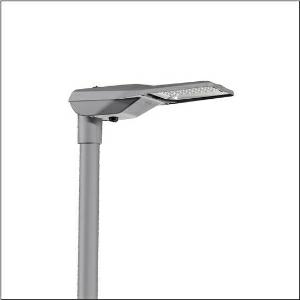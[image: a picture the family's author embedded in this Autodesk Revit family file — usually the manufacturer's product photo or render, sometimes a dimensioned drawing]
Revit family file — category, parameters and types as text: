
# Revit family: streetlight_sl_21_iq_mini___st1_0a_5xe2d21y08hb_5d36
name_source: partatom
category: Lighting Fixtures
units: mm (PartAtom-declared; Revit-internal decimal feet)

## family parameters
Cut with Voids When Loaded = No
Host = Face
Light Source = No
Part Type = Normal
Room Calculation Point = No
Round Connector Dimension = Use Diameter
Shared = No

## types (1)
- --- (1 x LED, 7820 lm, 71 W, 2200K)
    Apparent Load = 71 VA
    CIE Flux Codes = 37 72 97 100 100
    Color Rendering = 70
    Color Temperature = 2200K
    Default Elevation = 1800 mm
    Description = Streetlight SL 21 iQ mini, mast luminaire, primary light control with lens, of PMMA, primary optical cover: cover, of toughened safety glass, transparent, light distribution: ST1.0a, light emission: direct distribution, primary light characteristic: asymmetric, installation type: post-top, side-entry, LED, High Power LED, rated luminous flux: 7.820lm, luminous efficacy: 110lm/W, light colour: 722, colour temperature: 2200K, control gear: iQ-Street Remote, D4i with power reduction, control: pre-setting: logarithmic dimming characteristic, Street-Remote, Auto-Match, Temp-Guard, Lumen-Switch, Night-Set, Smart-Wire, Light-Fading, Desk-Remote (wireless, voltage-free reading and setting of iQ features in the workshop via application-optimized NFC function/RFID function), optimised constant luminous flux control (CLO 2.0), mains connection: 220..240V, AC, 50/60Hz, start of lifetime: 71W, end of service life: 75W, reduction: 30W, luminaire housing, of diecast aluminium, powder-coated, Siteco® metallic grey (DB 702S), corrosivity category C5 mid according to DIN EN ISO 12944, please order mast flange separately, inclination adjustable: 0°, 5°, 10°, 15°, sealing non-destructively replaceable, multi-level sealing system, length: 628mm, width: 235mm, height: 110mm, mast flange for spigot size: 42mm (side-entry): 5XC10008XM4, 60/48mm (side-entry/post-top): 5XC10108XM2, 76/60mm (side-entry/post-top): 5XC10108XM1, mounting height: 4..8m, Smart Interface below and above, protection rating (complete): IP66, insulation class (complete): insulation class II (safety insulation), certification: CE, ENEC, ENEC+, VDE, impact resistance: IK10, permissible operating ambient temperature for outdoor applications: -40..+50°C, standard-compliant lighting for roads and squares, packaging unit: 1 piece

Light Distribution: ST1.0a
    Height = 110 mm
    Lamp = 1 x LED
    Lamp Light Flux = 7820 lm
    Lamp Power = 71 W
    Lamp count = 1
    Length = 625 mm
    Luminous efficacy = 110 lm/W
    Manufacturer = Siteco
    ModVariant = No
    Model = 5XE2D21Y08HB
    Number of Poles = 1
    OnlyDefault = Yes
    Power Factor = 1
    Product Name = Streetlight SL 21 iQ mini | ST1.0a
    Product group = mast luminaire | pylon top
    ProductGroupID = 6100
    Protection Class = Protection class II
    Protection Degree = IP 66
    RLX_Detail_Level = 1
    RLX_Emergency_Light_Flux = 0 lm
    RLX_Emergency_Type = 0
    RLX_Emergency_Type_DB = No
    RlxData = <blob elided: 93973 chars, md5=9542672e>
    Socket = socket
    Standby Power = 0 W
    System Light Flux = 7820 lm
    System Power = 71 W
    Type Comments = factory setting: luminous flux: 100 % | dim-lin: 254 | 716 mA
    Type Image = l_1003514.jpg
    URL = http://relux.com
    VarID = @adj_136509
    Voltage = 0 V
    Weight = 0.00 kg
    Width = 234 mm

## geometry (parser evidence)
native form markers: Blend x4, Sweep x11
no freeform markers — native parametric forms only
